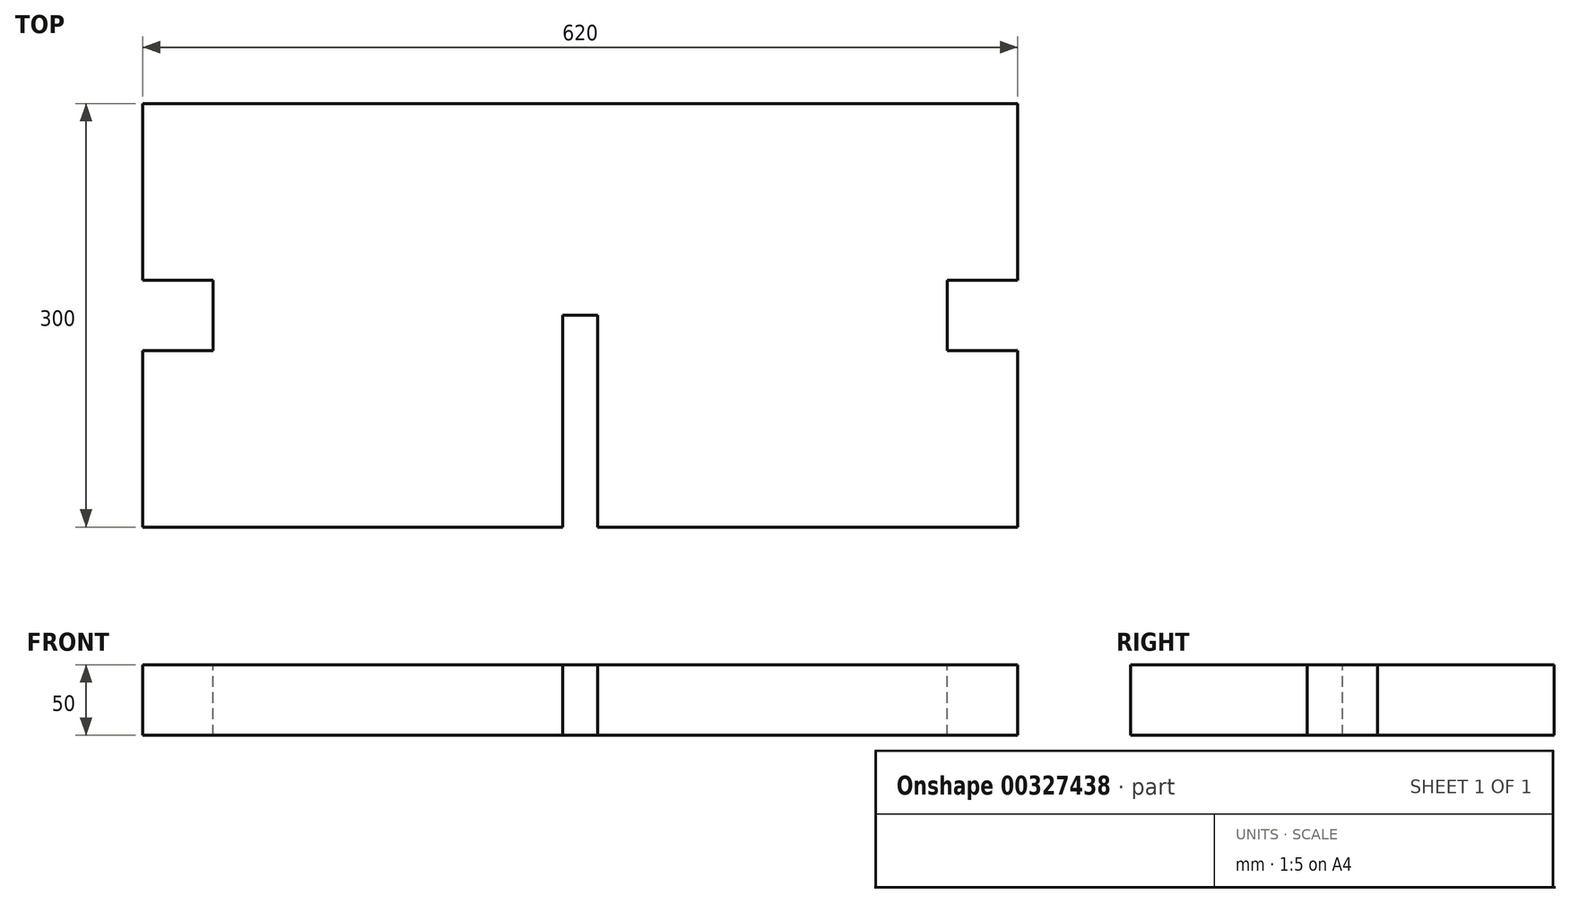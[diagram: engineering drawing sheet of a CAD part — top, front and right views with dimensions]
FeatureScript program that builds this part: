
annotation { "Feature Type Name" : "Feature", "Feature Type Description" : "" }
export const myFeature = defineFeature(function(context is Context, id is Id, definition is map)
    precondition{}
    {
        {
            var Q0;
            Q0=qCreatedBy(makeId("Front.planeOp"),FACE);
            var sketch = newSketch(context, id + "F0", { "sketchPlane" : qUnion([Q0])});
            skLineSegment(sketch, "E0.top", {"start": v(-331.57, 22.22) * mm, "end": v(-11.57, 22.22) * mm});
            skLineSegment(sketch, "E1", {"start": v(-331.57, 22.22) * mm, "end": v(-31.57, 22.22) * mm});
            skLineSegment(sketch, "E2", {"start": v(-31.57, 22.22) * mm, "end": v(-31.57, 72.22) * mm});
            skLineSegment(sketch, "E3", {"start": v(-11.57, 72.22) * mm, "end": v(-11.57, 22.22) * mm});
            skLineSegment(sketch, "E4", {"start": v(-31.57, 72.22) * mm, "end": v(288.43, 72.22) * mm});
            skLineSegment(sketch, "E5", {"start": v(-331.57, 22.22) * mm, "end": v(-331.57, 72.22) * mm});
            skLineSegment(sketch, "E6", {"start": v(288.43, 72.22) * mm, "end": v(288.43, 22.22) * mm});
            skLineSegment(sketch, "E7", {"start": v(-331.57, 72.22) * mm, "end": v(-31.57, 72.22) * mm});
            skLineSegment(sketch, "E8", {"start": v(-11.57, 22.22) * mm, "end": v(288.43, 22.22) * mm});
            skSolve(sketch);
        }
        {
            var Q0;
            Q0 = qSketchRegion(id + "F0", true);
            extrude(context, id + "F1", {"entities" : qUnion([Q0]), "depth" : 300 * mm});
        }
        {
            var Q0;
            Q0=makeQuery(id+"F1.opExtrude","SWEPT_FACE",FACE,{"disambiguationData":[OSD([sQuery(id+"F0.wireOp",EDGE,"E4"),sQuery(id+"F0.wireOp",EDGE,"E7")])]});
            var sketch = newSketch(context, id + "F2", { "sketchPlane" : qUnion([Q0])});
            skLineSegment(sketch, "E9", {"start": v(288.43, -175) * mm, "end": v(238.43, -175) * mm});
            skLineSegment(sketch, "E10", {"start": v(288.43, -125) * mm, "end": v(238.43, -125) * mm});
            skLineSegment(sketch, "E11", {"start": v(238.43, -175) * mm, "end": v(238.43, -125) * mm});
            skLineSegment(sketch, "E12.MirrorCS", {"start": v(-331.57, -175) * mm, "end": v(-281.57, -175) * mm});
            skLineSegment(sketch, "E13.MirrorCS", {"start": v(-281.57, -175) * mm, "end": v(-281.57, -125) * mm});
            skLineSegment(sketch, "E14.MirrorCS", {"start": v(-331.57, -125) * mm, "end": v(-281.57, -125) * mm});
            skPoint(sketch, "E15.orphan", {"position": v(219.55, -125) * mm});
            skLineSegment(sketch, "E16", {"start": v(-21.57, -300) * mm, "end": v(-9.07, -300) * mm});
            skLineSegment(sketch, "E17", {"start": v(-34.07, -300) * mm, "end": v(-34.07, -150) * mm});
            skPoint(sketch, "E18.orphan", {"position": v(-331.57, -150) * mm});
            skPoint(sketch, "E19.orphan", {"position": v(-21.57, -300) * mm});
            skPoint(sketch, "E20.end.orphan", {"position": v(-21.57, 0) * mm});
            skPoint(sketch, "E21.trimOffspring.end.orphan", {"position": v(288.43, -150) * mm});
            skLineSegment(sketch, "E22", {"start": v(-331.57, -300) * mm, "end": v(-34.07, -300) * mm});
            skLineSegment(sketch, "E23", {"start": v(-9.07, -300) * mm, "end": v(288.43, -300) * mm});
            skLineSegment(sketch, "E24", {"start": v(-9.07, -300) * mm, "end": v(-9.07, -150) * mm});
            skLineSegment(sketch, "E25", {"start": v(-9.07, -150) * mm, "end": v(-34.07, -150) * mm});
            skSolve(sketch);
        }
        {
            var Q0;
            {var subQ0=sQuery(id+"F2.wireOp",EDGE,"E12.MirrorCS");Q0=makeQuery(id+"F2.imprint","IMPRINT",FACE,{"disambiguationData":[TD([[makeQuery(id+"F2.imprint","IMPRINT",EDGE,{"derivedFrom":subQ0}),1.0]])]});}
            var Q1;
            {var subQ0=sQuery(id+"F2.wireOp",EDGE,"E9");Q1=makeQuery(id+"F2.imprint","IMPRINT",FACE,{"disambiguationData":[TD([[makeQuery(id+"F2.imprint","IMPRINT",EDGE,{"derivedFrom":subQ0}),-1.0]])]});}
            extrude(context, id + "F3", {"entities" : qUnion([Q0, Q1]), "operationType" : NewBodyOperationType.REMOVE, "oppositeDirection" : true, "depth" : 50 * mm});
        }
        {
            var Q0;
            {var subQ1=sQuery(id+"F2.wireOp",EDGE,"E16");Q0=makeQuery(id+"F2.imprint","IMPRINT",FACE,{"disambiguationData":[TD([[makeQuery(id+"F2.imprint","IMPRINT",EDGE,{"derivedFrom":subQ1}),1.0]])]});}
            extrude(context, id + "F4", {"entities" : qUnion([Q0]), "operationType" : NewBodyOperationType.REMOVE, "oppositeDirection" : true, "depth" : 50 * mm});
        }
    });
